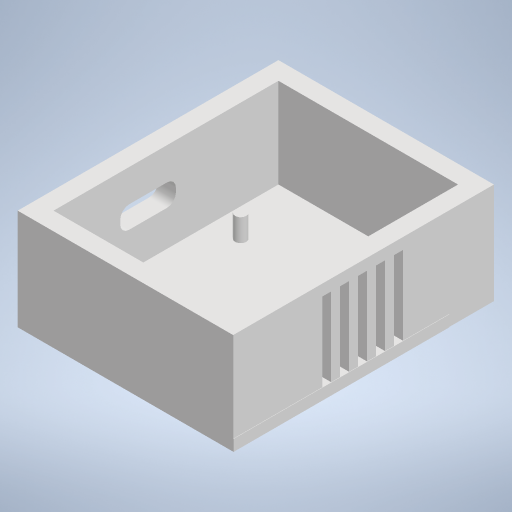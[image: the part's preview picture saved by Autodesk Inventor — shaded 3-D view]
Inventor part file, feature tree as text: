
AUTODESK INVENTOR PART (.ipt)
format: ipt  version: 2024 (Build 280153000, 153)  size: 317,440 bytes
history: native  units: mm
features: extrude x8, sketch x8, fillet x1, chamfer x1
ambient origin geometry x8: Origin, YZ Plane, XZ Plane, XY Plane, X Axis, Y Axis, Z Axis, Center Point
bodies: Volumenkörper1 (feature_tree)
feature tree (18):
  extrude  "Extrusion1"  Depth=48.1mm
  extrude  "Extrusion2"  Depth=4.0mm
  extrude  "Extrusion3"  Depth=4.0mm
  extrude  "Extrusion4"  Depth=4.0mm
  extrude  "Extrusion5"  Depth=4.0mm
  extrude  "Extrusion6"  Depth=2.5mm
  fillet  "Rundung1"  Radius=2.5mm
  extrude  "Extrusion7"  Depth=2.5mm TaperAngle=0.0deg
  extrude  "Extrusion8"  Depth=10.0mm TaperAngle=0.0deg
  chamfer  "Fasen1"  Distance=4.0mm
  sketch  "Skizze2"  dims[d6=48.1mm d7=48.1mm]
  sketch  "Skizze3"  dims[d8=4.0mm d9=4.0mm]
  sketch  "Skizze4"  dims[d10=4.0mm d11=4.0mm]
  sketch  "Skizze5"  dims[d12=2.5mm d13=0.0mm d14=4.0mm]
  sketch  "Skizze6"  dims[d15=4.0mm d16=4.0mm]
  sketch  "Skizze8"  dims[d17=4.0mm d18=2.5mm d19=2.5mm]
  sketch  "Skizze9"  dims[d20=2.5mm d21=2.5mm d22=0.0mm]
  sketch  "Skizze10"  dims[d23=2.5mm d24=0.0mm d25=10.0mm d26=0.0mm d27=4.0mm d28=4.0mm d29=4.0mm d30=4.0mm d31=20.0mm d32=0.0mm d33=20.0mm d34=0.0mm d35=2.0mm d36=2.5mm d38=2.0mm d39=2.0mm d40=2.0mm d41=2.0mm d42=2.0mm d43=2.0mm d44=2.0mm d45=2.0mm d46=2.0mm d47=20.0mm d48=0.0mm d49=20.0mm d50=5.0mm d51=10.0mm d52=4.0mm d53=2.0mm d54=2.0mm d55=0.0mm d56=2.0mm d57=2.0mm d58=45.0deg]
